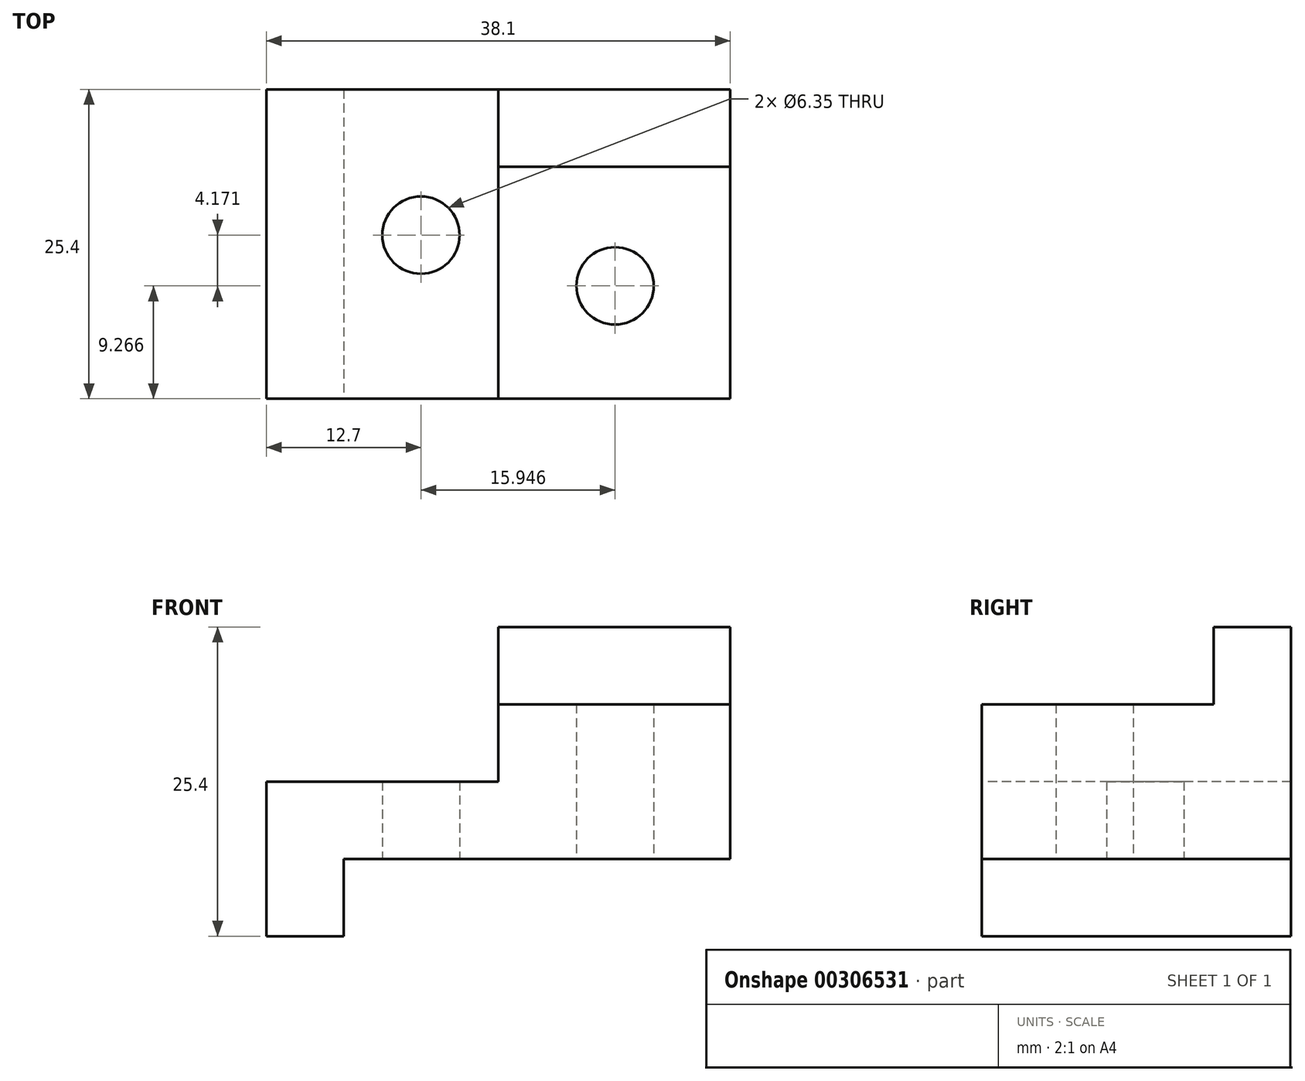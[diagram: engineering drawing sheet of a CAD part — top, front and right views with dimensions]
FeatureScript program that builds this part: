
annotation { "Feature Type Name" : "Feature", "Feature Type Description" : "" }
export const myFeature = defineFeature(function(context is Context, id is Id, definition is map)
    precondition{}
    {
        {
            var Q0;
            Q0=qCreatedBy(makeId("Front.planeOp"),FACE);
            var sketch = newSketch(context, id + "F0", { "sketchPlane" : qUnion([Q0])});
            skLineSegment(sketch, "E0", {"start": v(0, 0) * mm, "end": v(38.1, 0) * mm});
            skLineSegment(sketch, "E1", {"start": v(38.1, 0) * mm, "end": v(38.1, 25.4) * mm});
            skLineSegment(sketch, "E2", {"start": v(38.1, 25.4) * mm, "end": v(0, 25.4) * mm});
            skLineSegment(sketch, "E3", {"start": v(0, 25.4) * mm, "end": v(0, 0) * mm});
            skSolve(sketch);
        }
        {
            var Q0;
            Q0 = qSketchRegion(id + "F0", true);
            extrude(context, id + "F1", {"entities" : qUnion([Q0]), "depth" : 25.4 * mm});
        }
        {
            var Q0;
            Q0=makeQuery(id+"F1.opExtrude","CAP_FACE",FACE,{"disambiguationData":[OSD([sQuery(id+"F0.wireOp",EDGE,"E0"),sQuery(id+"F0.wireOp",EDGE,"E1"),sQuery(id+"F0.wireOp",EDGE,"E2"),sQuery(id+"F0.wireOp",EDGE,"E3")])],"isStart":false});
            var sketch = newSketch(context, id + "F2", { "sketchPlane" : qUnion([Q0])});
            skLineSegment(sketch, "E4", {"start": v(6.35, 0) * mm, "end": v(6.35, 6.35) * mm});
            skLineSegment(sketch, "E5", {"start": v(6.35, 6.35) * mm, "end": v(38.1, 6.35) * mm});
            skLineSegment(sketch, "E6", {"start": v(38.1, 6.35) * mm, "end": v(38.1, 0) * mm});
            skLineSegment(sketch, "E7", {"start": v(38.1, 0) * mm, "end": v(6.35, 0) * mm});
            skLineSegment(sketch, "E8", {"start": v(0, 12.7) * mm, "end": v(19.05, 12.7) * mm});
            skLineSegment(sketch, "E9", {"start": v(19.05, 12.7) * mm, "end": v(19.05, 25.4) * mm});
            skLineSegment(sketch, "E10", {"start": v(19.05, 25.4) * mm, "end": v(0, 25.4) * mm});
            skLineSegment(sketch, "E11", {"start": v(0, 25.4) * mm, "end": v(0, 12.7) * mm});
            skSolve(sketch);
        }
        {
            var Q0;
            Q0 = qSketchRegion(id + "F2", true);
            extrude(context, id + "F3", {"entities" : qUnion([Q0]), "operationType" : NewBodyOperationType.REMOVE, "endBound" : BoundingType.THROUGH_ALL, "oppositeDirection" : true, "depth" : 25.4 * mm});
        }
        {
            var Q0;
            Q0=makeQuery(id+"F1.opExtrude","SWEPT_FACE",FACE,{"disambiguationData":[OSD([sQuery(id+"F0.wireOp",EDGE,"E1")])]});
            var sketch = newSketch(context, id + "F4", { "sketchPlane" : qUnion([Q0])});
            skLineSegment(sketch, "E12", {"start": v(-25.4, 19.05) * mm, "end": v(-6.35, 19.05) * mm});
            skLineSegment(sketch, "E13", {"start": v(-6.35, 19.05) * mm, "end": v(-6.35, 25.4) * mm});
            skLineSegment(sketch, "E14", {"start": v(-6.35, 25.4) * mm, "end": v(-25.4, 25.4) * mm});
            skLineSegment(sketch, "E15", {"start": v(-25.4, 25.4) * mm, "end": v(-25.4, 19.05) * mm});
            skSolve(sketch);
        }
        {
            var Q0;
            Q0 = qSketchRegion(id + "F4", true);
            extrude(context, id + "F5", {"entities" : qUnion([Q0]), "operationType" : NewBodyOperationType.REMOVE, "endBound" : BoundingType.THROUGH_ALL, "oppositeDirection" : true, "depth" : 25.4 * mm});
        }
        {
            var Q0;
            Q0=qCreatedBy(makeId("Top.planeOp"),FACE);
            var sketch = newSketch(context, id + "F6", { "sketchPlane" : qUnion([Q0])});
            skCircle(sketch, "E16", {"center": v(12.7, -11.96) * mm, "radius": 3.18 * mm});
            skCircle(sketch, "E17", {"center": v(28.65, -16.13) * mm, "radius": 3.18 * mm});
            skSolve(sketch);
        }
        {
            var Q0;
            Q0 = qSketchRegion(id + "F6", true);
            extrude(context, id + "F7", {"entities" : qUnion([Q0]), "operationType" : NewBodyOperationType.REMOVE, "endBound" : BoundingType.THROUGH_ALL, "depth" : 25.4 * mm});
        }
    });
